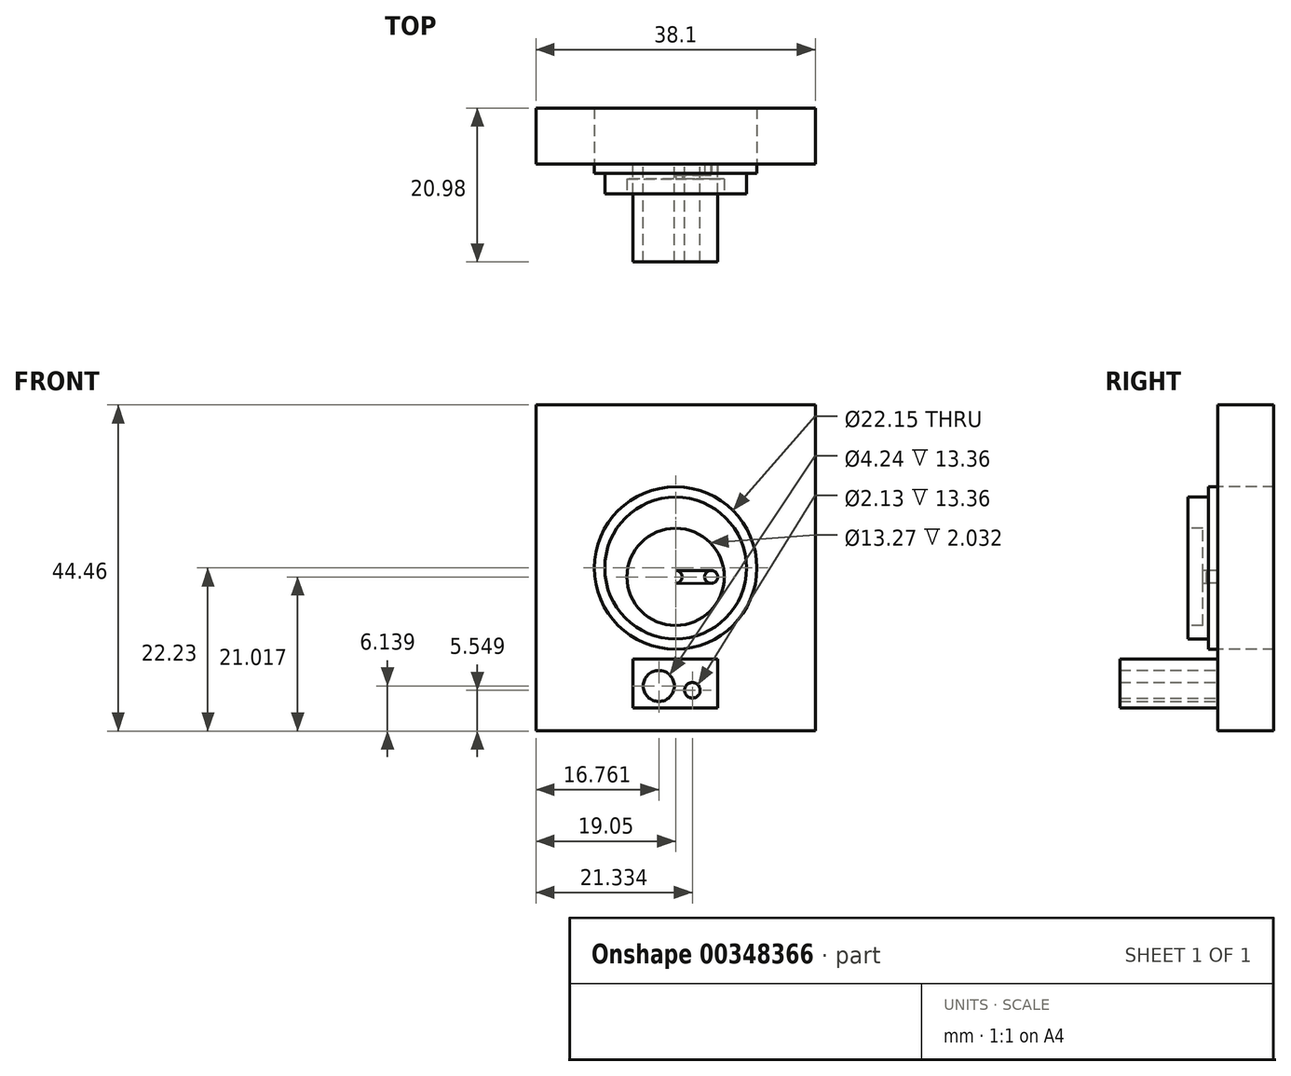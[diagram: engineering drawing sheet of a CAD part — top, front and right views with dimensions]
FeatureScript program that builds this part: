
annotation { "Feature Type Name" : "Feature", "Feature Type Description" : "" }
export const myFeature = defineFeature(function(context is Context, id is Id, definition is map)
    precondition{}
    {
        {
            var Q0;
            Q0=qCreatedBy(makeId("Front.planeOp"),FACE);
            var sketch = newSketch(context, id + "F0", { "sketchPlane" : qUnion([Q0])});
            skCircle(sketch, "E0", {"center": v(0, 0) * mm, "radius": 9.66 * mm});
            skLineSegment(sketch, "E1", {"start": v(0, 9.66) * mm, "end": v(0, 5.42) * mm});
            skCircle(sketch, "E2", {"center": v(0, -1.21) * mm, "radius": 6.64 * mm});
            skCircle(sketch, "E3", {"center": v(0, 0) * mm, "radius": 11.07 * mm});
            skLineSegment(sketch, "E4.bottom", {"start": v(19.05, -22.22) * mm, "end": v(-19.05, -22.23) * mm});
            skLineSegment(sketch, "E4.top", {"start": v(19.05, 22.23) * mm, "end": v(-19.05, 22.22) * mm});
            skLineSegment(sketch, "E4.left", {"start": v(19.05, -22.22) * mm, "end": v(19.05, 22.23) * mm});
            skLineSegment(sketch, "E4.right", {"start": v(-19.05, -22.23) * mm, "end": v(-19.05, 22.23) * mm});
            skSolve(sketch);
        }
        {
            var Q0;
            Q0=makeQuery(id+"F0.imprint","IMPRINT",FACE,{"disambiguationData":[TD([[makeQuery(id+"F0.imprint","IMPRINT",EDGE,{"derivedFrom":sQuery(id+"F0.wireOp",EDGE,"E0")}),1.0]])]});
            var Q1;
            Q1=makeQuery(id+"F0.imprint","IMPRINT",FACE,{"disambiguationData":[TD([[makeQuery(id+"F0.imprint","IMPRINT",EDGE,{"derivedFrom":sQuery(id+"F0.wireOp",EDGE,"E2")}),1.0]])]});
            extrude(context, id + "F1", {"entities" : qUnion([Q0, Q1]), "depth" : 4.08 * mm});
        }
        {
            var Q0;
            Q0=makeQuery(id+"F0.imprint","IMPRINT",FACE,{"disambiguationData":[TD([[makeQuery(id+"F0.imprint","IMPRINT",EDGE,{"derivedFrom":sQuery(id+"F0.wireOp",EDGE,"E0")}),-1.0]])]});
            extrude(context, id + "F2", {"entities" : qUnion([Q0]), "operationType" : NewBodyOperationType.ADD, "depth" : 1.26 * mm});
        }
        {
            var Q0;
            Q0=makeQuery(id+"F1.opExtrude","CAP_FACE",FACE,{"disambiguationData":[OSD([sQuery(id+"F0.wireOp",EDGE,"E0")])],"isStart":false});
            var sketch = newSketch(context, id + "F3", { "sketchPlane" : qUnion([Q0])});
            skCircle(sketch, "E5.0", {"center": v(0, -1.21) * mm, "radius": 6.64 * mm});
            skSolve(sketch);
        }
        {
            var Q0;
            Q0=makeQuery(id+"F3.imprint","IMPRINT",FACE,{"disambiguationData":[TD([[makeQuery(id+"F3.imprint","IMPRINT",EDGE,{"derivedFrom":sQuery(id+"F3.wireOp",EDGE,"E5.0")}),1.0]])]});
            extrude(context, id + "F4", {"entities" : qUnion([Q0]), "operationType" : NewBodyOperationType.REMOVE, "oppositeDirection" : true, "depth" : 2.03 * mm});
        }
        {
            var Q0;
            Q0=makeQuery(id+"F4.boolean.opBoolean","COPY",FACE,{"derivedFrom":makeQuery(id+"F4.opExtrude","CAP_FACE",FACE,{"disambiguationData":[OSD([sQuery(id+"F3.wireOp",EDGE,"E5.0")])],"isStart":false})});
            var sketch = newSketch(context, id + "F5", { "sketchPlane" : qUnion([Q0])});
            skCircle(sketch, "E6.0", {"center": v(0, -1.21) * mm, "radius": 6.64 * mm});
            skCircle(sketch, "E7", {"center": v(0, -1.21) * mm, "radius": 0.89 * mm});
            skLineSegment(sketch, "E8", {"start": v(0, -1.21) * mm, "end": v(4.85, -1.21) * mm});
            skCircle(sketch, "E9", {"center": v(4.85, -1.21) * mm, "radius": 0.89 * mm});
            skLineSegment(sketch, "E10", {"start": v(4.91, -2.1) * mm, "end": v(0, -2.1) * mm});
            skLineSegment(sketch, "E11", {"start": v(0, -0.32) * mm, "end": v(4.91, -0.32) * mm});
            skSolve(sketch);
        }
        {
            var Q0;
            {var subQ0=sQuery(id+"F5.wireOp",EDGE,"E9");var subQ1=makeQuery(id+"F5.imprint","INTERSECT",VERTEX,{"derivedFrom":[sQuery(id+"F5.wireOp",EDGE,"E8"),subQ0]});Q0=makeQuery(id+"F5.imprint","IMPRINT",FACE,{"disambiguationData":[TD([[makeQuery(id+"F5.imprint","IMPRINT",EDGE,{"disambiguationData":[TD([[subQ1,1.0]])],"derivedFrom":subQ0}),1.0]])]});}
            var Q1;
            {var subQ0=sQuery(id+"F5.wireOp",EDGE,"E11");var subQ1=sQuery(id+"F5.wireOp",EDGE,"E7");var subQ2=makeQuery(id+"F5.imprint","INTERSECT",VERTEX,{"derivedFrom":[subQ1,subQ0]});Q1=makeQuery(id+"F5.imprint","IMPRINT",FACE,{"disambiguationData":[TD([[makeQuery(id+"F5.imprint","IMPRINT",EDGE,{"disambiguationData":[TD([[subQ2,1.0]])],"derivedFrom":subQ1}),-1.0]])]});}
            var Q2;
            {var subQ0=sQuery(id+"F5.wireOp",EDGE,"E10");var subQ1=sQuery(id+"F5.wireOp",EDGE,"E7");var subQ2=makeQuery(id+"F5.imprint","INTERSECT",VERTEX,{"derivedFrom":[subQ1,subQ0]});Q2=makeQuery(id+"F5.imprint","IMPRINT",FACE,{"disambiguationData":[TD([[makeQuery(id+"F5.imprint","IMPRINT",EDGE,{"disambiguationData":[TD([[subQ2,-1.0]])],"derivedFrom":subQ1}),-1.0]])]});}
            var Q3;
            {var subQ0=sQuery(id+"F5.wireOp",EDGE,"E7");var subQ3=makeQuery(id+"F5.imprint","IMPRINT",VERTEX,{"derivedFrom":subQ0});Q3=makeQuery(id+"F5.imprint","IMPRINT",FACE,{"disambiguationData":[TD([[makeQuery(id+"F5.imprint","IMPRINT",EDGE,{"disambiguationData":[TD([[subQ3,1.0]])],"derivedFrom":subQ0}),1.0]])]});}
            extrude(context, id + "F6", {"entities" : qUnion([Q0, Q1, Q2, Q3]), "operationType" : NewBodyOperationType.REMOVE, "oppositeDirection" : true, "depth" : 0.5 * mm});
        }
        {
            var Q0;
            Q0=makeQuery(id+"F0.imprint","IMPRINT",FACE,{"disambiguationData":[TD([[makeQuery(id+"F0.imprint","IMPRINT",EDGE,{"derivedFrom":sQuery(id+"F0.wireOp",EDGE,"E3")}),-1.0]])]});
            extrude(context, id + "F7", {"entities" : qUnion([Q0]), "oppositeDirection" : true, "depth" : 7.62 * mm});
        }
        {
            var Q0;
            Q0=makeQuery(id+"F6.boolean.opBoolean","COPY",FACE,{"derivedFrom":makeQuery(id+"F6.opExtrude","CAP_FACE",FACE,{"disambiguationData":[OSD([sQuery(id+"F5.wireOp",EDGE,"E7"),sQuery(id+"F5.wireOp",EDGE,"E9"),sQuery(id+"F5.wireOp",EDGE,"E10"),sQuery(id+"F5.wireOp",EDGE,"E11")])],"isStart":false})});
            var sketch = newSketch(context, id + "F8", { "sketchPlane" : qUnion([Q0])});
            skArc(sketch, "E12.0", {"start": v(4.91, -2.1) * mm, "mid": v(5.74, -1.18) * mm, "end": v(4.85, -0.32) * mm});
            skCircle(sketch, "E13", {"center": v(4.85, -1.21) * mm, "radius": 0.89 * mm});
            skSolve(sketch);
        }
        {
            var Q0;
            {var subQ0=sQuery(id+"F8.wireOp",EDGE,"E13");var subQ1=makeQuery(id+"F8.imprint","INTERSECT",VERTEX,{"derivedFrom":[makeQuery(id+"F6.boolean.opBoolean","COPY",EDGE,{"derivedFrom":makeQuery(id+"F6.opExtrude","CAP_EDGE",EDGE,{"disambiguationData":[OSD([sQuery(id+"F5.wireOp",EDGE,"E11")])],"isStart":false})}),subQ0]});Q0=makeQuery(id+"F8.imprint","IMPRINT",FACE,{"disambiguationData":[TD([[makeQuery(id+"F8.imprint","IMPRINT",EDGE,{"disambiguationData":[TD([[subQ1,-1.0]])],"derivedFrom":subQ0}),1.0]])]});}
            extrude(context, id + "F9", {"entities" : qUnion([Q0]), "operationType" : NewBodyOperationType.REMOVE, "oppositeDirection" : true, "depth" : 27.94 * mm});
        }
        {
            var Q0;
            Q0=makeQuery(id+"F0.imprint","IMPRINT",FACE,{"disambiguationData":[TD([[makeQuery(id+"F0.imprint","IMPRINT",EDGE,{"derivedFrom":sQuery(id+"F0.wireOp",EDGE,"E3")}),-1.0]])]});
            var sketch = newSketch(context, id + "F10", { "sketchPlane" : qUnion([Q0])});
            skCircle(sketch, "E14.0", {"center": v(0, 0) * mm, "radius": 9.66 * mm});
            skCircle(sketch, "E15.0", {"center": v(0, 0) * mm, "radius": 11.07 * mm});
            skCircle(sketch, "E16", {"center": v(-2.29, -16.1) * mm, "radius": 2.12 * mm});
            skCircle(sketch, "E17", {"center": v(3.27, -15.92) * mm, "radius": 1.06 * mm});
            skLineSegment(sketch, "E18.bottom", {"start": v(5.72, -19.07) * mm, "end": v(-5.8, -19.07) * mm});
            skLineSegment(sketch, "E18.top", {"start": v(5.72, -12.41) * mm, "end": v(-5.8, -12.41) * mm});
            skLineSegment(sketch, "E18.left", {"start": v(5.72, -19.07) * mm, "end": v(5.72, -12.41) * mm});
            skLineSegment(sketch, "E18.right", {"start": v(-5.8, -19.07) * mm, "end": v(-5.8, -12.41) * mm});
            skSolve(sketch);
        }
        {
            var Q0;
            Q0=makeQuery(id+"F0.imprint","IMPRINT",FACE,{"disambiguationData":[TD([[makeQuery(id+"F0.imprint","IMPRINT",EDGE,{"derivedFrom":sQuery(id+"F0.wireOp",EDGE,"E3")}),-1.0]])]});
            var sketch = newSketch(context, id + "F11", { "sketchPlane" : qUnion([Q0])});
            skCircle(sketch, "E19.0", {"center": v(-2.29, -16.1) * mm, "radius": 2.12 * mm});
            skLineSegment(sketch, "E20.0", {"start": v(5.72, -12.41) * mm, "end": v(-5.8, -12.41) * mm});
            skLineSegment(sketch, "E21.0", {"start": v(5.72, -19.07) * mm, "end": v(5.72, -12.41) * mm});
            skCircle(sketch, "E22.0", {"center": v(2.28, -16.68) * mm, "radius": 1.06 * mm});
            skLineSegment(sketch, "E23.0", {"start": v(5.72, -19.07) * mm, "end": v(-5.8, -19.07) * mm});
            skLineSegment(sketch, "E24.0", {"start": v(-5.8, -19.07) * mm, "end": v(-5.8, -12.41) * mm});
            skCircle(sketch, "E25", {"center": v(-2.29, -16.1) * mm, "radius": 2.11 * mm});
            skSolve(sketch);
        }
        {
            var Q0;
            Q0 = qSketchRegion(id + "F11", true);
            extrude(context, id + "F12", {"entities" : qUnion([Q0]), "operationType" : NewBodyOperationType.ADD, "depth" : 13.36 * mm});
        }
    });
